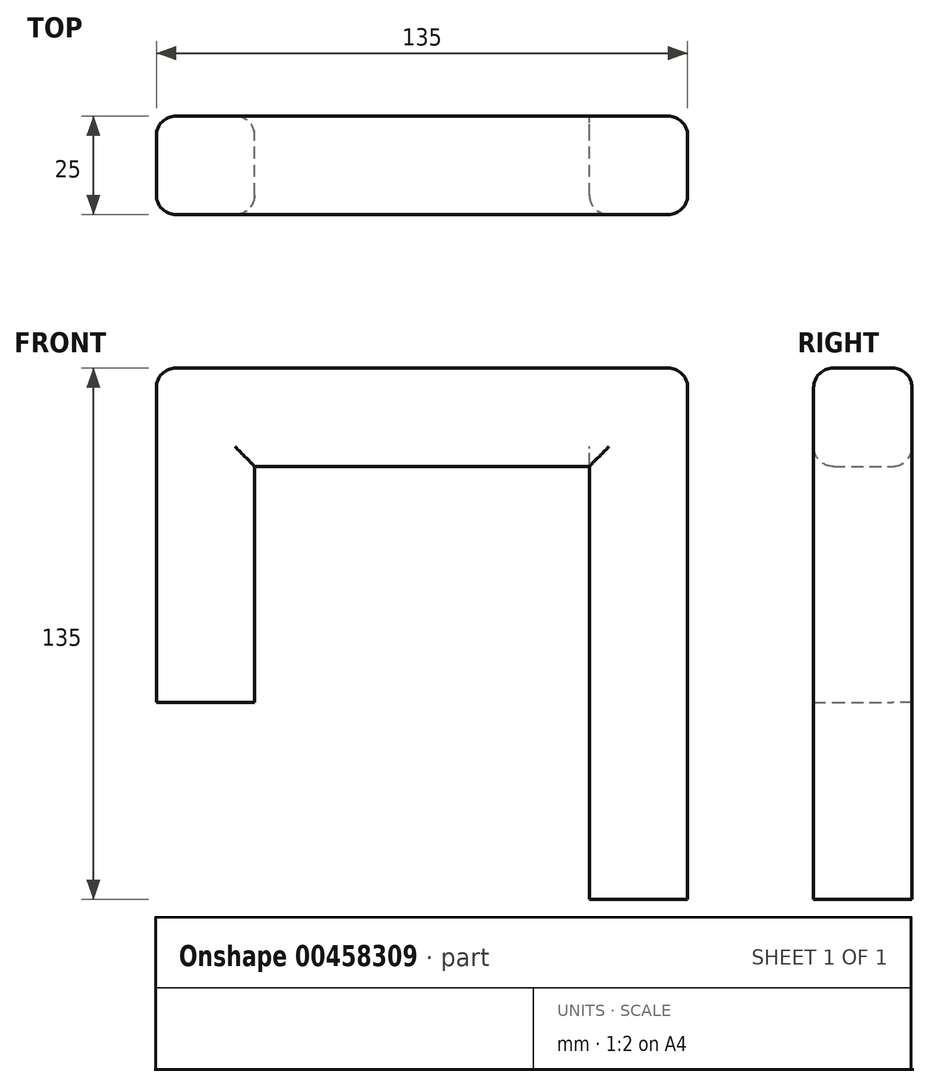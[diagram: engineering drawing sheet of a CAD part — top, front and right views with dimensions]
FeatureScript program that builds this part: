
annotation { "Feature Type Name" : "Feature", "Feature Type Description" : "" }
export const myFeature = defineFeature(function(context is Context, id is Id, definition is map)
    precondition{}
    {
        {
            var Q0;
            Q0=qCreatedBy(makeId("Top.planeOp"),FACE);
            var sketch = newSketch(context, id + "F0", { "sketchPlane" : qUnion([Q0])});
            skLineSegment(sketch, "E0.bottom", {"start": v(0, 0) * mm, "end": v(25, 0) * mm});
            skLineSegment(sketch, "E0.top", {"start": v(0, 25) * mm, "end": v(25, 25) * mm});
            skLineSegment(sketch, "E0.left", {"start": v(0, 0) * mm, "end": v(0, 25) * mm});
            skLineSegment(sketch, "E0.right", {"start": v(25, 0) * mm, "end": v(25, 25) * mm});
            skSolve(sketch);
        }
        {
            var Q0;
            Q0=makeQuery(id+"F0.imprint","IMPRINT",FACE,{"disambiguationData":[TD([[makeQuery(id+"F0.imprint","IMPRINT",EDGE,{"derivedFrom":sQuery(id+"F0.wireOp",EDGE,"E0.bottom")}),1.0]])]});
            extrude(context, id + "F1", {"entities" : qUnion([Q0]), "depth" : 60 * mm});
        }
        {
            var Q0;
            Q0=makeQuery(id+"F1.opExtrude","SWEPT_FACE",FACE,{"disambiguationData":[OSD([sQuery(id+"F0.wireOp",EDGE,"E0.right")])]});
            var sketch = newSketch(context, id + "F2", { "sketchPlane" : qUnion([Q0])});
            skLineSegment(sketch, "E1.bottom", {"start": v(0, 60) * mm, "end": v(25, 60) * mm});
            skLineSegment(sketch, "E1.top", {"start": v(0, 35) * mm, "end": v(25, 35) * mm});
            skLineSegment(sketch, "E1.left", {"start": v(0, 60) * mm, "end": v(0, 35) * mm});
            skLineSegment(sketch, "E1.right", {"start": v(25, 60) * mm, "end": v(25, 35) * mm});
            skSolve(sketch);
        }
        {
            var Q0;
            Q0=makeQuery(id+"F2.imprint","IMPRINT",FACE,{"disambiguationData":[TD([[makeQuery(id+"F2.imprint","IMPRINT",EDGE,{"derivedFrom":sQuery(id+"F2.wireOp",EDGE,"E1.bottom")}),-1.0]])]});
            extrude(context, id + "F3", {"entities" : qUnion([Q0]), "operationType" : NewBodyOperationType.ADD, "depth" : 60 * mm});
        }
        {
            var Q0;
            Q0=makeQuery(id+"F1.opExtrude","CAP_FACE",FACE,{"disambiguationData":[OSD([sQuery(id+"F0.wireOp",EDGE,"E0.bottom"),sQuery(id+"F0.wireOp",EDGE,"E0.top"),sQuery(id+"F0.wireOp",EDGE,"E0.left"),sQuery(id+"F0.wireOp",EDGE,"E0.right")])],"isStart":true});
            extrude(context, id + "F4", {"entities" : qUnion([Q0]), "operationType" : NewBodyOperationType.ADD, "depth" : 25 * mm});
        }
        {
            var Q0;
            Q0=makeQuery(id+"F3.opExtrude","CAP_FACE",FACE,{"disambiguationData":[OSD([sQuery(id+"F2.wireOp",EDGE,"E1.bottom"),sQuery(id+"F2.wireOp",EDGE,"E1.top"),sQuery(id+"F2.wireOp",EDGE,"E1.left"),sQuery(id+"F2.wireOp",EDGE,"E1.right")])],"isStart":false});
            extrude(context, id + "F5", {"entities" : qUnion([Q0]), "operationType" : NewBodyOperationType.ADD, "depth" : 50 * mm});
        }
        {
            var Q0;
            {var subQ0=sQuery(id+"F2.wireOp",EDGE,"E1.top");Q0=makeQuery(id+"F5.boolean.opBoolean","MERGE",FACE,{"derivedFrom":[makeQuery(id+"F3.opExtrude","SWEPT_FACE",FACE,{"disambiguationData":[OSD([subQ0])]}),makeQuery(id+"F5.opExtrude","SWEPT_FACE",FACE,{"disambiguationData":[OSD([subQ0])]})]});}
            var sketch = newSketch(context, id + "F6", { "sketchPlane" : qUnion([Q0])});
            skLineSegment(sketch, "E2.bottom", {"start": v(135, 0) * mm, "end": v(110, 0) * mm});
            skLineSegment(sketch, "E2.top", {"start": v(135, -25) * mm, "end": v(110, -25) * mm});
            skLineSegment(sketch, "E2.left", {"start": v(135, 0) * mm, "end": v(135, -25) * mm});
            skLineSegment(sketch, "E2.right", {"start": v(110, 0) * mm, "end": v(110, -25) * mm});
            skSolve(sketch);
        }
        {
            var Q0;
            Q0=makeQuery(id+"F6.imprint","IMPRINT",FACE,{"disambiguationData":[TD([[makeQuery(id+"F6.imprint","IMPRINT",EDGE,{"derivedFrom":sQuery(id+"F6.wireOp",EDGE,"E2.bottom")}),1.0]])]});
            extrude(context, id + "F7", {"entities" : qUnion([Q0]), "operationType" : NewBodyOperationType.ADD, "depth" : 110 * mm});
        }
        {
            var Q0;
            {var subQ0=sQuery(id+"F2.wireOp",EDGE,"E1.left");var subQ1=sQuery(id+"F2.wireOp",EDGE,"E1.bottom");Q0=makeQuery(id+"F5.boolean.opBoolean","MERGE",EDGE,{"derivedFrom":[makeQuery(id+"F3.boolean.opBoolean","MERGE",EDGE,{"derivedFrom":[makeQuery(id+"F1.opExtrude","CAP_EDGE",EDGE,{"disambiguationData":[OSD([sQuery(id+"F0.wireOp",EDGE,"E0.bottom")])],"isStart":false}),makeQuery(id+"F3.opExtrude","SWEPT_EDGE",EDGE,{"disambiguationData":[OSD([subQ1,subQ0])]})]}),makeQuery(id+"F5.opExtrude","SWEPT_EDGE",EDGE,{"disambiguationData":[OSD([subQ1,subQ0])]})]});}
            var Q1;
            {var subQ0=sQuery(id+"F2.wireOp",EDGE,"E1.right");var subQ1=sQuery(id+"F2.wireOp",EDGE,"E1.bottom");Q1=makeQuery(id+"F5.boolean.opBoolean","MERGE",EDGE,{"derivedFrom":[makeQuery(id+"F3.boolean.opBoolean","MERGE",EDGE,{"derivedFrom":[makeQuery(id+"F1.opExtrude","CAP_EDGE",EDGE,{"disambiguationData":[OSD([sQuery(id+"F0.wireOp",EDGE,"E0.top")])],"isStart":false}),makeQuery(id+"F3.opExtrude","SWEPT_EDGE",EDGE,{"disambiguationData":[OSD([subQ1,subQ0])]})]}),makeQuery(id+"F5.opExtrude","SWEPT_EDGE",EDGE,{"disambiguationData":[OSD([subQ1,subQ0])]})]});}
            var Q2;
            {var subQ0=sQuery(id+"F0.wireOp",EDGE,"E0.right");var subQ1=sQuery(id+"F0.wireOp",EDGE,"E0.bottom");Q2=makeQuery(id+"F4.boolean.opBoolean","MERGE",EDGE,{"derivedFrom":[makeQuery(id+"F1.opExtrude","SWEPT_EDGE",EDGE,{"disambiguationData":[OSD([subQ1,subQ0])]}),makeQuery(id+"F4.opExtrude","SWEPT_EDGE",EDGE,{"disambiguationData":[OSD([subQ1,subQ0])]})]});}
            var Q3;
            {var subQ0=sQuery(id+"F0.wireOp",EDGE,"E0.right");var subQ1=sQuery(id+"F0.wireOp",EDGE,"E0.top");Q3=makeQuery(id+"F4.boolean.opBoolean","MERGE",EDGE,{"derivedFrom":[makeQuery(id+"F1.opExtrude","SWEPT_EDGE",EDGE,{"disambiguationData":[OSD([subQ1,subQ0])]}),makeQuery(id+"F4.opExtrude","SWEPT_EDGE",EDGE,{"disambiguationData":[OSD([subQ1,subQ0])]})]});}
            var Q4;
            {var subQ0=sQuery(id+"F0.wireOp",EDGE,"E0.left");var subQ1=sQuery(id+"F0.wireOp",EDGE,"E0.bottom");Q4=makeQuery(id+"F4.boolean.opBoolean","MERGE",EDGE,{"derivedFrom":[makeQuery(id+"F1.opExtrude","SWEPT_EDGE",EDGE,{"disambiguationData":[OSD([subQ1,subQ0])]}),makeQuery(id+"F4.opExtrude","SWEPT_EDGE",EDGE,{"disambiguationData":[OSD([subQ1,subQ0])]})]});}
            var Q5;
            {var subQ0=sQuery(id+"F0.wireOp",EDGE,"E0.left");var subQ1=sQuery(id+"F0.wireOp",EDGE,"E0.top");Q5=makeQuery(id+"F4.boolean.opBoolean","MERGE",EDGE,{"derivedFrom":[makeQuery(id+"F1.opExtrude","SWEPT_EDGE",EDGE,{"disambiguationData":[OSD([subQ1,subQ0])]}),makeQuery(id+"F4.opExtrude","SWEPT_EDGE",EDGE,{"disambiguationData":[OSD([subQ1,subQ0])]})]});}
            var Q6;
            {var subQ0=sQuery(id+"F2.wireOp",EDGE,"E1.left");var subQ1=sQuery(id+"F2.wireOp",EDGE,"E1.top");var subQ2=sQuery(id+"F0.wireOp",EDGE,"E0.right");var subQ3=sQuery(id+"F0.wireOp",EDGE,"E0.bottom");Q6=makeQuery(id+"F5.boolean.opBoolean","MERGE",EDGE,{"derivedFrom":[makeQuery(id+"F3.opExtrude","SWEPT_EDGE",EDGE,{"disambiguationData":[OSD([subQ3,subQ2,subQ1,subQ0])]}),makeQuery(id+"F5.opExtrude","SWEPT_EDGE",EDGE,{"disambiguationData":[OSD([subQ3,subQ2,subQ1,subQ0])]})]});}
            var Q7;
            Q7=makeQuery(id+"F7.opExtrude","SWEPT_EDGE",EDGE,{"disambiguationData":[OSD([sQuery(id+"F0.wireOp",EDGE,"E0.bottom"),sQuery(id+"F0.wireOp",EDGE,"E0.right"),sQuery(id+"F2.wireOp",EDGE,"E1.top"),sQuery(id+"F2.wireOp",EDGE,"E1.left"),sQuery(id+"F6.wireOp",EDGE,"E2.bottom"),sQuery(id+"F6.wireOp",EDGE,"E2.right")])]});
            var Q8;
            Q8=makeQuery(id+"F7.boolean.opBoolean","MERGE",EDGE,{"derivedFrom":[makeQuery(id+"F5.opExtrude","CAP_EDGE",EDGE,{"disambiguationData":[OSD([sQuery(id+"F2.wireOp",EDGE,"E1.left")])],"isStart":false}),makeQuery(id+"F7.opExtrude","SWEPT_EDGE",EDGE,{"disambiguationData":[OSD([sQuery(id+"F6.wireOp",EDGE,"E2.bottom"),sQuery(id+"F6.wireOp",EDGE,"E2.left")])]})]});
            var Q9;
            Q9=makeQuery(id+"F7.boolean.opBoolean","MERGE",EDGE,{"derivedFrom":[makeQuery(id+"F5.opExtrude","CAP_EDGE",EDGE,{"disambiguationData":[OSD([sQuery(id+"F2.wireOp",EDGE,"E1.right")])],"isStart":false}),makeQuery(id+"F7.opExtrude","SWEPT_EDGE",EDGE,{"disambiguationData":[OSD([sQuery(id+"F6.wireOp",EDGE,"E2.top"),sQuery(id+"F6.wireOp",EDGE,"E2.left")])]})]});
            var Q10;
            Q10=makeQuery(id+"F5.opExtrude","CAP_EDGE",EDGE,{"disambiguationData":[OSD([sQuery(id+"F2.wireOp",EDGE,"E1.bottom")])],"isStart":false});
            var Q11;
            Q11=makeQuery(id+"F1.opExtrude","CAP_EDGE",EDGE,{"disambiguationData":[OSD([sQuery(id+"F0.wireOp",EDGE,"E0.left")])],"isStart":false});
            var Q12;
            {var subQ0=sQuery(id+"F2.wireOp",EDGE,"E1.right");var subQ1=sQuery(id+"F2.wireOp",EDGE,"E1.top");var subQ2=sQuery(id+"F0.wireOp",EDGE,"E0.right");var subQ3=sQuery(id+"F0.wireOp",EDGE,"E0.top");Q12=makeQuery(id+"F5.boolean.opBoolean","MERGE",EDGE,{"derivedFrom":[makeQuery(id+"F3.opExtrude","SWEPT_EDGE",EDGE,{"disambiguationData":[OSD([subQ3,subQ2,subQ1,subQ0])]}),makeQuery(id+"F5.opExtrude","SWEPT_EDGE",EDGE,{"disambiguationData":[OSD([subQ3,subQ2,subQ1,subQ0])]})]});}
            fillet(context, id + "F8", {"entities" : qUnion([Q0, Q1, Q2, Q3, Q4, Q5, Q6, Q7, Q8, Q9, Q10, Q11, Q12]), "radius" : 5 * mm, "tangentPropagation" : true, "allowEdgeOverflow" : false});
        }
    });
